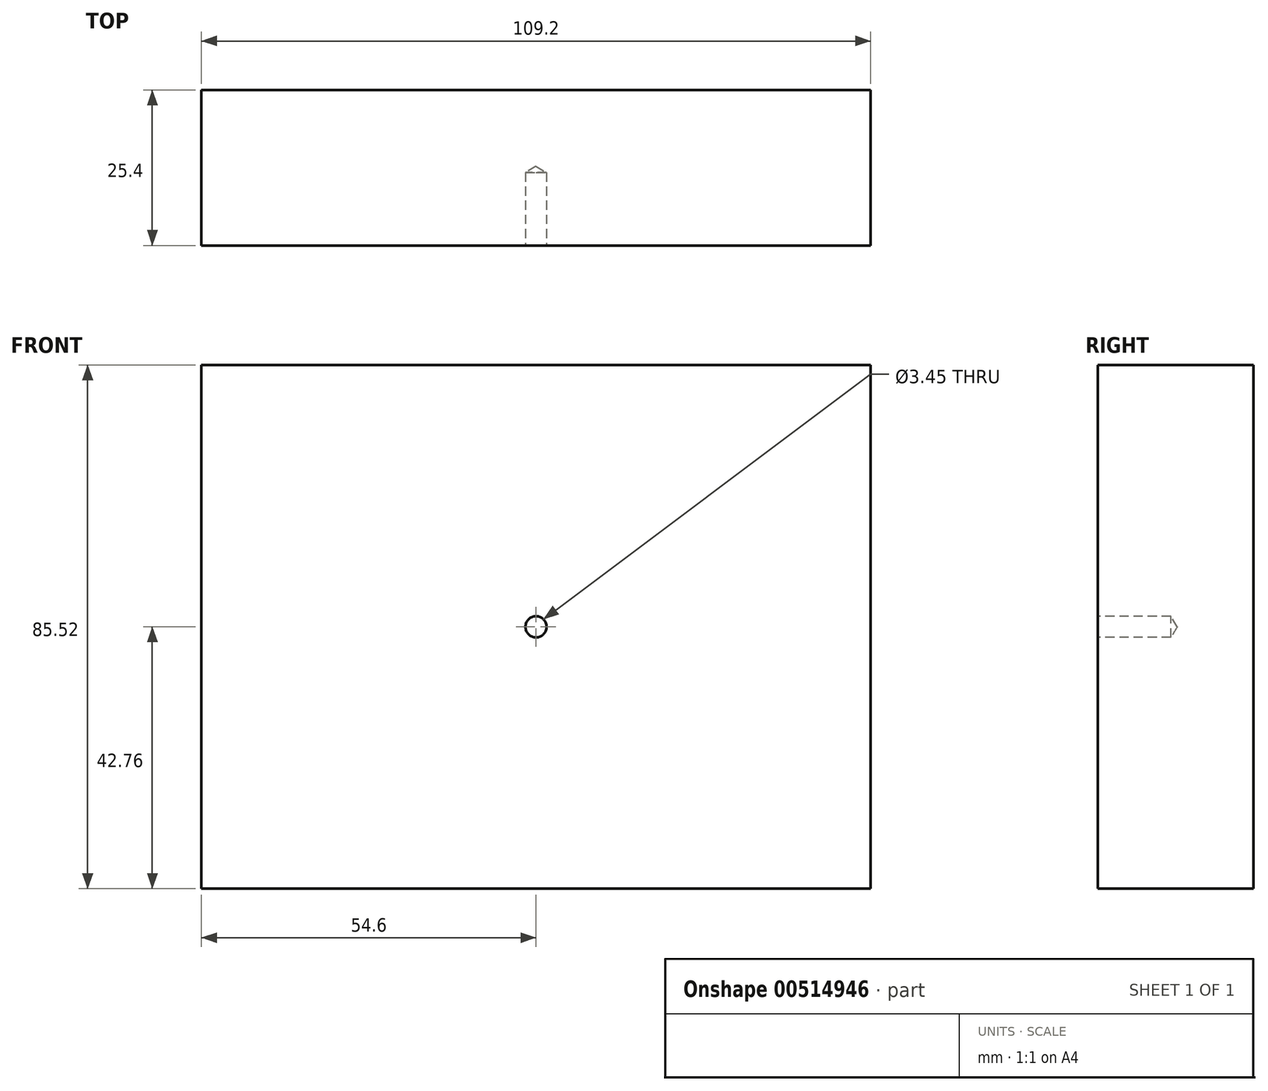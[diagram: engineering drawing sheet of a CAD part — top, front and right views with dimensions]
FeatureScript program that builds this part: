
annotation { "Feature Type Name" : "Feature", "Feature Type Description" : "" }
export const myFeature = defineFeature(function(context is Context, id is Id, definition is map)
    precondition{}
    {
        {
            var Q0;
            Q0=qCreatedBy(makeId("Front.planeOp"),FACE);
            var sketch = newSketch(context, id + "F0", { "sketchPlane" : qUnion([Q0])});
            skLineSegment(sketch, "E0.bottom", {"start": v(54.6, -42.76) * mm, "end": v(-54.6, -42.76) * mm});
            skLineSegment(sketch, "E0.top", {"start": v(54.6, 42.76) * mm, "end": v(-54.6, 42.76) * mm});
            skLineSegment(sketch, "E0.left", {"start": v(54.6, -42.76) * mm, "end": v(54.6, 42.76) * mm});
            skLineSegment(sketch, "E0.right", {"start": v(-54.6, -42.76) * mm, "end": v(-54.6, 42.76) * mm});
            skPoint(sketch, "E0.middle", {"position": v(0, 0) * mm});
            skSolve(sketch);
        }
        {
            var Q0;
            Q0 = qSketchRegion(id + "F0", true);
            extrude(context, id + "F1", {"entities" : qUnion([Q0]), "depth" : 25.4 * mm, "offsetDistance" : 25.4 * mm});
        }
        {
            var Q0;
            Q0=makeQuery(id+"F1.opExtrude","CAP_FACE",FACE,{"disambiguationData":[OSD([sQuery(id+"F0.wireOp",EDGE,"E0.bottom"),sQuery(id+"F0.wireOp",EDGE,"E0.top"),sQuery(id+"F0.wireOp",EDGE,"E0.left"),sQuery(id+"F0.wireOp",EDGE,"E0.right")])],"isStart":false});
            var sketch = newSketch(context, id + "F2", { "sketchPlane" : qUnion([Q0])});
            skPoint(sketch, "E1", {"position": v(0, 0) * mm});
            skSolve(sketch);
        }
        {
            var Q0;
            Q0=sQuery(id+"F2.wireOp",VERTEX,"E1");
            var Q1;
            Q1=makeQuery(id+"F1.opExtrude","SWEPT_BODY",BODY,{"disambiguationData":[OSD([sQuery(id+"F0.wireOp",EDGE,"E0.bottom"),sQuery(id+"F0.wireOp",EDGE,"E0.top"),sQuery(id+"F0.wireOp",EDGE,"E0.left"),sQuery(id+"F0.wireOp",EDGE,"E0.right")])]});
            hole(context, id + "F3", {"style" : HoleStyle.SIMPLE, "endStyle" : HoleEndStyle.BLIND, "standardTappedOrClearance" : lookupTablePath({ "standard" : "ANSI", "engagement" : "75%", "pitch" : "32 tpi", "size" : "#8", "type" : "Tapped" }), "standardBlindInLast" : lookupTablePath({ "standard" : "ANSI", "engagement" : "75%", "pitch" : "32 tpi", "size" : "#8", "type" : "Tapped" }), "holeDiameter" : 3.45 * mm, "showTappedDepth" : true, "holeDepth" : 11.9 * mm, "tappedDepth" : 9.52 * mm, "tapClearance" : 3, "startFromSketch" : true, "locations" : qUnion([Q0]), "scope" : qUnion([Q1]), "majorDiameter" : 4.17 * mm});
        }
    });
